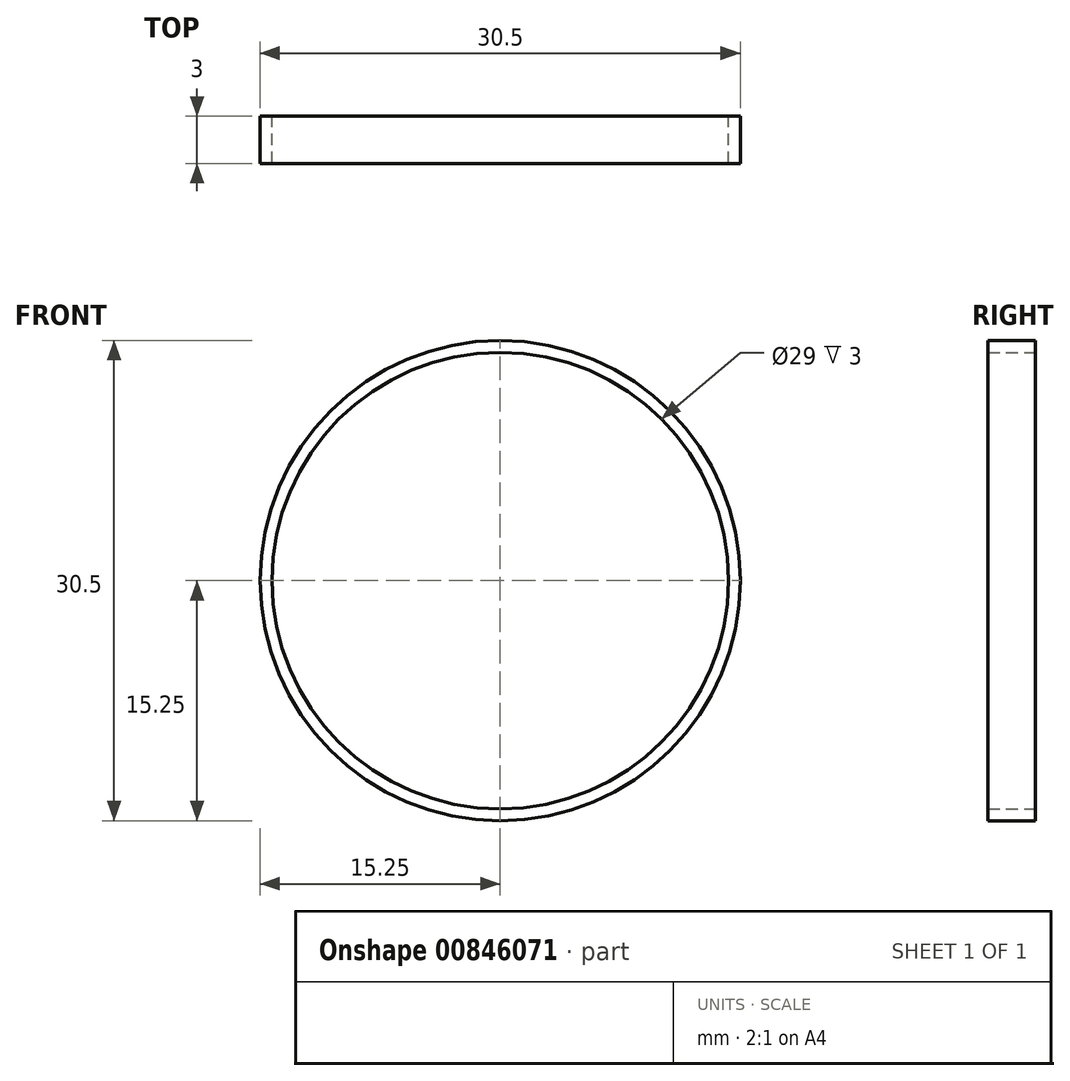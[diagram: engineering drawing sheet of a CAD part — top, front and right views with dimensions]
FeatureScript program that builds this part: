
annotation { "Feature Type Name" : "Feature", "Feature Type Description" : "" }
export const myFeature = defineFeature(function(context is Context, id is Id, definition is map)
    precondition{}
    {
        {
            var Q0;
            Q0=qCreatedBy(makeId("Front.planeOp"),FACE);
            var sketch = newSketch(context, id + "F0", { "sketchPlane" : qUnion([Q0])});
            skCircle(sketch, "E0", {"center": v(0, 0) * mm, "radius": 14.5 * mm});
            skCircle(sketch, "E1", {"center": v(0, 0) * mm, "radius": 15.25 * mm});
            skCircle(sketch, "E2", {"center": v(0, 0) * mm, "radius": 15.5 * mm});
            skCircle(sketch, "E3", {"center": v(0, 0) * mm, "radius": 15.75 * mm});
            skCircle(sketch, "E4", {"center": v(0, 0) * mm, "radius": 18.25 * mm});
            skFitSpline(sketch, "E5", {"points": [v(-10.72, 14.76) * mm, v(-7.25, 16.76) * mm], "startDerivative": vector(2.84, 7.09) * mm, "endDerivative": vector(7.56, -1.09) * mm});
            skFitSpline(sketch, "E6", {"points": [v(10.72, -14.76) * mm, v(7.25, -16.76) * mm], "startDerivative": vector(-2.84, -7.09) * mm, "endDerivative": vector(-7.56, 1.09) * mm});
            skFitSpline(sketch, "E7", {"points": [v(-10.72, 14.76) * mm, v(-7.25, 16.76) * mm], "startDerivative": vector(2.84, 7.09) * mm, "endDerivative": vector(7.56, -1.09) * mm});
            skFitSpline(sketch, "E8", {"points": [v(-10.72, -14.76) * mm, v(-7.25, -16.76) * mm], "startDerivative": vector(2.84, -7.09) * mm, "endDerivative": vector(7.56, 1.09) * mm});
            skFitSpline(sketch, "E9", {"points": [v(7.42, 16.66) * mm, v(10.89, 14.66) * mm], "startDerivative": vector(7.56, 1.09) * mm, "endDerivative": vector(2.84, -7.09) * mm});
            skSolve(sketch);
        }
        {
            var Q0;
            Q0=sQuery(id+"F0.wireOp",EDGE,"E4");
            extrude(context, id + "F1", {"bodyType" : ToolBodyType.SURFACE, "surfaceEntities" : qUnion([Q0]), "depth" : 8 * mm, "offsetDistance" : 25 * mm});
        }
        {
            var Q0;
            Q0=makeQuery(id+"F0.imprint","IMPRINT",FACE,{"disambiguationData":[TD([[makeQuery(id+"F0.imprint","IMPRINT",EDGE,{"derivedFrom":sQuery(id+"F0.wireOp",EDGE,"E0")}),-1.0]])]});
            extrude(context, id + "F2", {"entities" : qUnion([Q0]), "depth" : 3 * mm, "offsetDistance" : 25 * mm});
        }
        {
            var Q0;
            Q0=sQuery(id+"F0.wireOp",EDGE,"E2");
            extrude(context, id + "F3", {"bodyType" : ToolBodyType.SURFACE, "surfaceEntities" : qUnion([Q0]), "depth" : 7 * mm, "offsetDistance" : 25 * mm});
        }
    });
